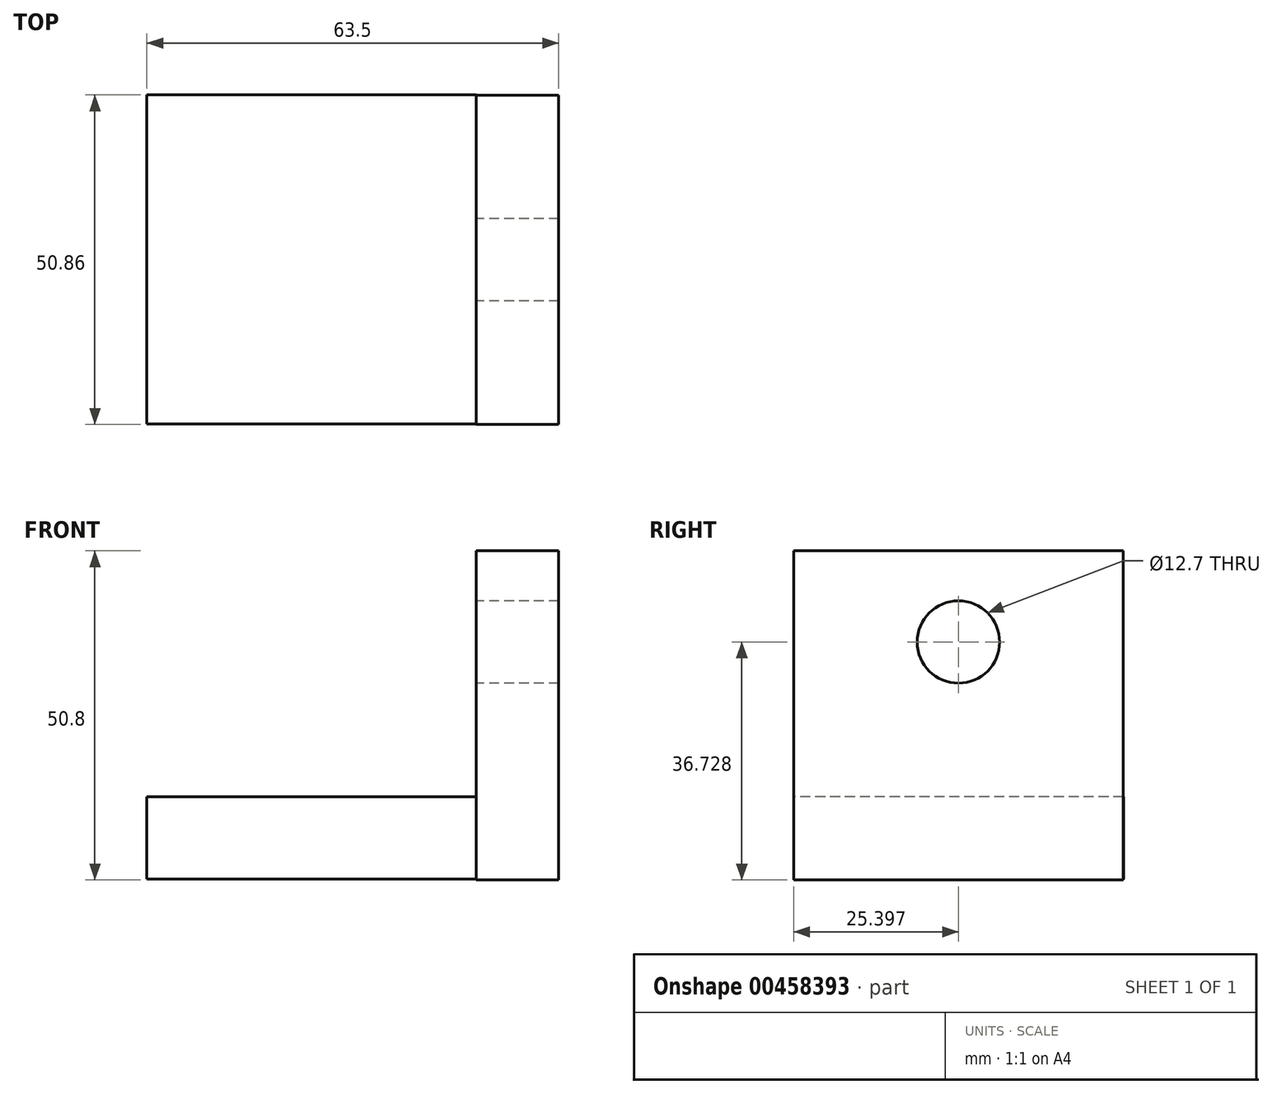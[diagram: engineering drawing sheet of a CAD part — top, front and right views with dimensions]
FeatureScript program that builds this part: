
annotation { "Feature Type Name" : "Feature", "Feature Type Description" : "" }
export const myFeature = defineFeature(function(context is Context, id is Id, definition is map)
    precondition{}
    {
        {
            var Q0;
            Q0=qCreatedBy(makeId("Right.planeOp"),FACE);
            var sketch = newSketch(context, id + "F0", { "sketchPlane" : qUnion([Q0])});
            skLineSegment(sketch, "E0.bottom", {"start": v(28.64, 31.42) * mm, "end": v(-22.16, 31.42) * mm});
            skLineSegment(sketch, "E0.top", {"start": v(28.64, -19.38) * mm, "end": v(-22.16, -19.38) * mm});
            skLineSegment(sketch, "E0.left", {"start": v(28.64, 31.42) * mm, "end": v(28.64, -19.38) * mm});
            skLineSegment(sketch, "E0.right", {"start": v(-22.16, 31.42) * mm, "end": v(-22.16, -19.38) * mm});
            skSolve(sketch);
        }
        {
            var Q0;
            Q0=qCreatedBy(makeId("Right.planeOp"),FACE);
            var sketch = newSketch(context, id + "F1", { "sketchPlane" : qUnion([Q0])});
            skLineSegment(sketch, "E1", {"start": v(28.7, -19.24) * mm, "end": v(28.7, -6.54) * mm});
            skLineSegment(sketch, "E2", {"start": v(28.7, -6.54) * mm, "end": v(-22.1, -6.54) * mm});
            skLineSegment(sketch, "E3", {"start": v(-22.1, -6.54) * mm, "end": v(-22.1, -19.24) * mm});
            skLineSegment(sketch, "E4", {"start": v(-22.1, -19.24) * mm, "end": v(28.7, -19.24) * mm});
            skSolve(sketch);
        }
        {
            var Q0;
            Q0 = qSketchRegion(id + "F0", true);
            extrude(context, id + "F2", {"entities" : qUnion([Q0]), "depth" : 12.7 * mm});
        }
        {
            var Q0;
            Q0 = qSketchRegion(id + "F1", true);
            extrude(context, id + "F3", {"entities" : qUnion([Q0]), "operationType" : NewBodyOperationType.ADD, "oppositeDirection" : true, "depth" : 50.8 * mm});
        }
        {
            var Q0;
            Q0=qCreatedBy(makeId("Right.planeOp"),FACE);
            var sketch = newSketch(context, id + "F4", { "sketchPlane" : qUnion([Q0])});
            skCircle(sketch, "E5", {"center": v(3.24, 17.35) * mm, "radius": 6.35 * mm});
            skSolve(sketch);
        }
        {
            var Q0;
            Q0 = qSketchRegion(id + "F4", true);
            extrude(context, id + "F5", {"entities" : qUnion([Q0]), "operationType" : NewBodyOperationType.REMOVE, "endBound" : BoundingType.THROUGH_ALL, "depth" : 25.4 * mm});
        }
    });
